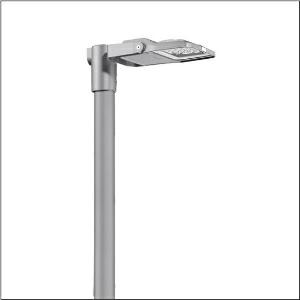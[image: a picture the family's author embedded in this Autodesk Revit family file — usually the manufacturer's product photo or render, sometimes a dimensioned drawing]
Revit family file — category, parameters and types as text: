
# Revit family: floodlight_fl_21_iq_micro___pl33t_5xa7761a4f3a_749b
name_source: partatom
category: Lighting Fixtures
units: mm (PartAtom-declared; Revit-internal decimal feet)

## family parameters
Cut with Voids When Loaded = No
Host = Face
Light Source = No
Part Type = Normal
Room Calculation Point = No
Round Connector Dimension = Use Diameter
Shared = No

## types (1)
- --- (1 x LED, 3050 lm, 23.1 W, 4000K)
    Apparent Load = 23 VA
    CIE Flux Codes = 26 75 99 100 100
    Color Rendering = 70
    Color Temperature = 4000K
    Default Elevation = 1800 mm
    Description = Floodlight FL 21 iQ micro, floodlight, primary light control with lens, of PMMA, primary optical cover: protective disc, of toughened safety glass, transparent, light distribution: PL33T, light emission: direct distribution, installation type: surface-mounted, LED, High Power LED, rated luminous flux: 3.050lm, luminous efficacy: 132lm/W, light colour: 740, colour temperature: 4000K, control: optimised constant luminous flux control (CLO 2.0), Desk-Remote (wireless, voltage-free reading and setting of iQ features in the workshop via application-optimized NFC function/RFID function), Light-Fading, Smart-Wire, Night-Set, Lumen-Switch, Temp-Guard, Auto-Match, with terminal, 6-pole, mains connection: 220..240V, AC, 50/60Hz, start of lifetime: 23W, end of service life: 24W, reduction: 11W, luminaire housing, of diecast aluminium, powder-coated, Siteco® metallic grey (DB 702S), corrosivity category C5 mid according to DIN EN ISO 12944, sealing non-destructively replaceable, please order mast flange separately, mast bracket, of steel, galvanised, powder-coated, Siteco® metallic grey (DB 702S), protection rating (complete): IP66, insulation class (complete): insulation class II (safety insulation), certification: CE, ENEC, VDE, protection symbol: D, impact resistance: IK07, permissible operating ambient temperature: -40..+40°C, permissible operating ambient temperature for outdoor applications: -40..+50°C, standard: DIN EN 12944, LABS conformity tested according to VDMA 24364:2018-05, packaging unit: 1 piece

Light Distribution: PL33T
    Height = 65 mm
    Lamp = 1 x LED
    Lamp Light Flux = 3050 lm
    Lamp Power = 23.1 W
    Lamp count = 1
    Length = 312 mm
    Luminous efficacy = 132 lm/W
    Manufacturer = Siteco
    ModVariant = No
    Model = 5XA7761A4F3A
    Number of Poles = 1
    OnlyDefault = Yes
    Power Factor = 1
    Product Name = Floodlight FL 21 iQ micro | PL33T
    Product group = floodlight | pylon annexe
    ProductGroupID = 6200
    Protection Class = Protection class II
    Protection Degree = IP 66
    RLX_Detail_Level = 1
    RLX_Emergency_Light_Flux = 0 lm
    RLX_Emergency_Type = 0
    RLX_Emergency_Type_DB = No
    RlxData = <blob elided: 101821 chars, md5=b29c80e7>
    Socket = socket
    Standby Power = 0 W
    System Light Flux = 3050 lm
    System Power = 23 W
    Type Comments = factory setting: luminous flux: 100 % | dim-lin: 254 | 455 mA
    Type Image = l_1007121.jpg
    URL = http://relux.com
    VarID = @adj_080601
    Voltage = 0 V
    Weight = 0.00 kg
    Width = 230 mm

## geometry (parser evidence)
native form markers: Blend x4, Sweep x13
no freeform markers — native parametric forms only
